# Revit family: STS-125 Извещатель охранный_RV17_LOD400
name_source: partatom
category: Датчики
revit_build: Autodesk Revit 2017 (Build: 20170118_1100(x64)
units: mm (PartAtom-declared; Revit-internal decimal feet)

## family parameters
Всегда вертикально = Нет
На основе рабочей плоскости = Нет
Общий = Нет
При загрузке вырезать с полостями = Нет
Размер круглого соединителя = Использовать диаметр
Сохранять ориентацию аннотаций = Нет
Тип детали = Нормальный
Точка расчета площади = Нет

## types (1)
- STS-125 Извещатель охранный
    ADSK_URL страницы изделия = https://stilsoft.ru
    ADSK_Единица измерения = шт.
    ADSK_Завод-изготовитель = ООО «Основа Безопасности»
    ADSK_Количество = 1
    ADSK_Марка = СТВФ.426479.046
    ADSK_Масса = 0.5
    ADSK_Наименование = Извещатель охранный STS-125
    ADSK_Размер_Высота = 145 мм
    ADSK_Размер_Длина = 155 мм
    ADSK_Размер_Ширина = 75 мм
    d_короба = 20 мм
    Вероятность обнаружения нарушителя, не менее = 0.98
    Время восстановления дежурного режима после выдачи тревожного извещения, не более, с = 10
    Время технической готовности, не более, с = 30
    Выдача тревожного извещения при вскрытии корпуса = да
    Диапазон обнаруживаемых скоростей нарушителя, м/с = от 0,3 до 3,0
    Диапазон рабочих температур, °С = от –40 до +50
    Длительность сообщения, с = 2
    Защита от попадания внутрь твердых тел (пыли) и воды = IP 54
    Информативность извещателя по шине RS-485 = 8
    Информативность извещателя по шлейфу = 5
    Информационный выход = релейный, RS-485
    Максимальная дальность обнаружения при угле обзора в горизонтальной плоскости 90°, не менее, м = 12
    Напряжение электропитания постоянного тока, В = 8-30
    Наработка на ложное срабатывание не менее, ч = 1200
    Поворот извещателя по вертикали/горизонтали, не менее, град. = ±15/±90
    Помехоустойчивость изделия от солнца и источников освещения, питающихся от источников постоянного тока, не менее, лк = 30000
    Помехоустойчивость изделия от электроосветительных приборов, питающихся от сети переменного тока, не менее, лк = 2000
    Режим работы = непрерывный
    Ток, потребляемый в дежурном состоянии и режиме «Тревога», при номинальном напряжении, не более, мА = 20
